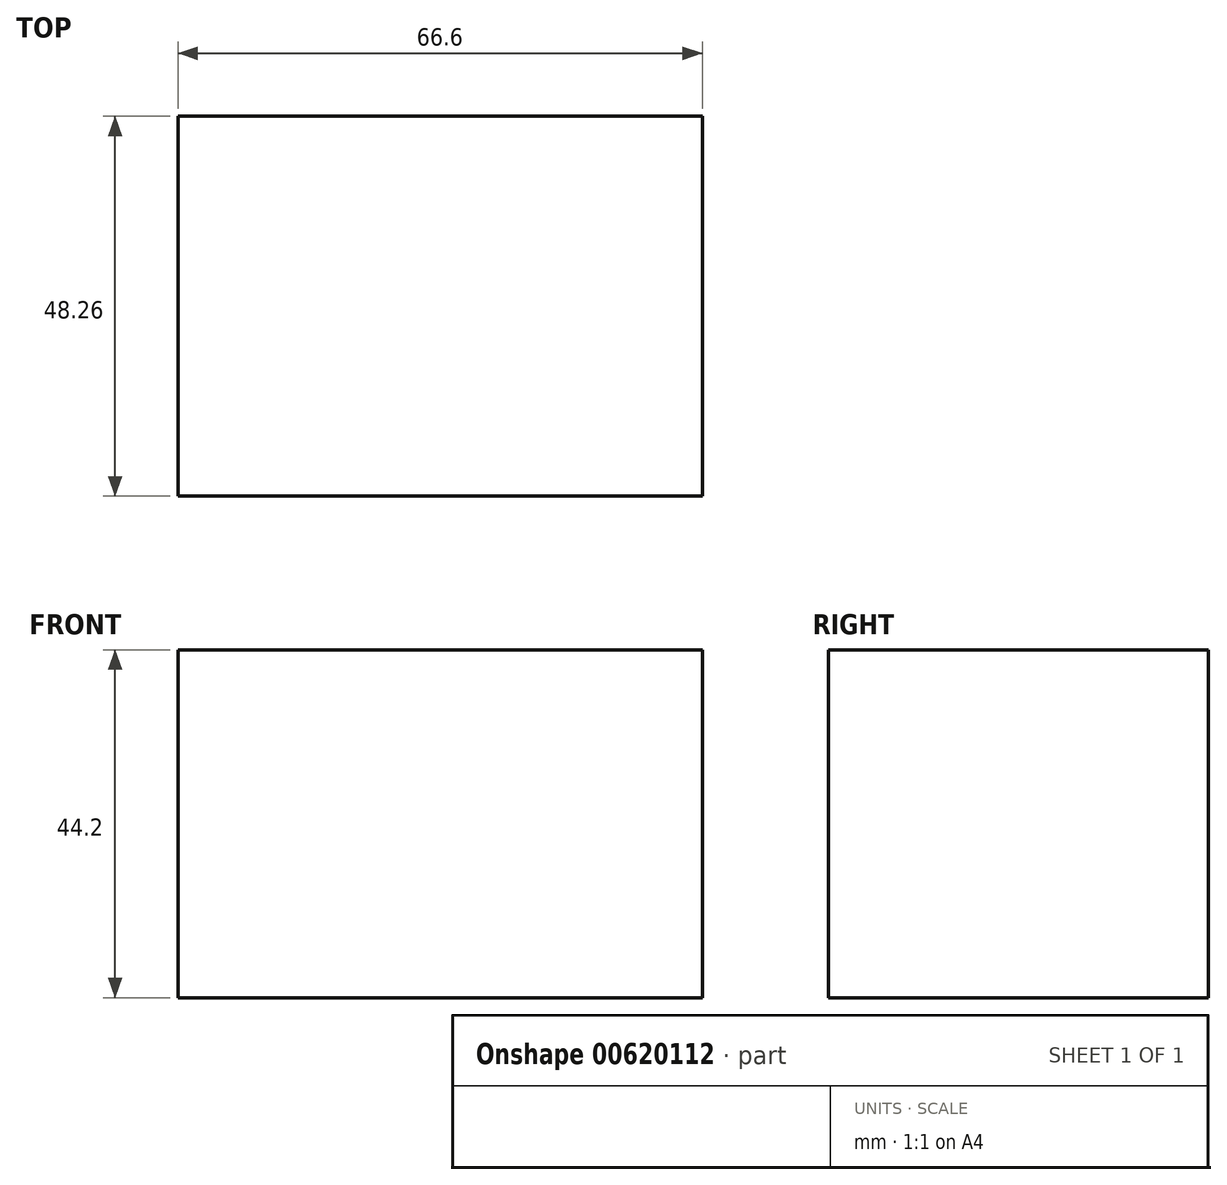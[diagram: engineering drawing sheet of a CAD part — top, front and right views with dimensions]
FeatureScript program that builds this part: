
annotation { "Feature Type Name" : "Feature", "Feature Type Description" : "" }
export const myFeature = defineFeature(function(context is Context, id is Id, definition is map)
    precondition{}
    {
        {
            var Q0;
            Q0=qCreatedBy(makeId("Front.planeOp"),FACE);
            var sketch = newSketch(context, id + "F0", { "sketchPlane" : qUnion([Q0])});
            skLineSegment(sketch, "E0", {"start": v(0, 44.2) * mm, "end": v(0, 0) * mm});
            skLineSegment(sketch, "E1", {"start": v(0, 44.2) * mm, "end": v(66.6, 44.2) * mm});
            skLineSegment(sketch, "E2", {"start": v(66.6, 44.2) * mm, "end": v(66.6, 0) * mm});
            skLineSegment(sketch, "E3", {"start": v(0, 0) * mm, "end": v(66.6, 0) * mm});
            skSolve(sketch);
        }
        {
            var Q0;
            Q0 = qSketchRegion(id + "F0", true);
            extrude(context, id + "F1", {"entities" : qUnion([Q0]), "depth" : 48.26 * mm, "offsetDistance" : 25.4 * mm});
        }
    });
